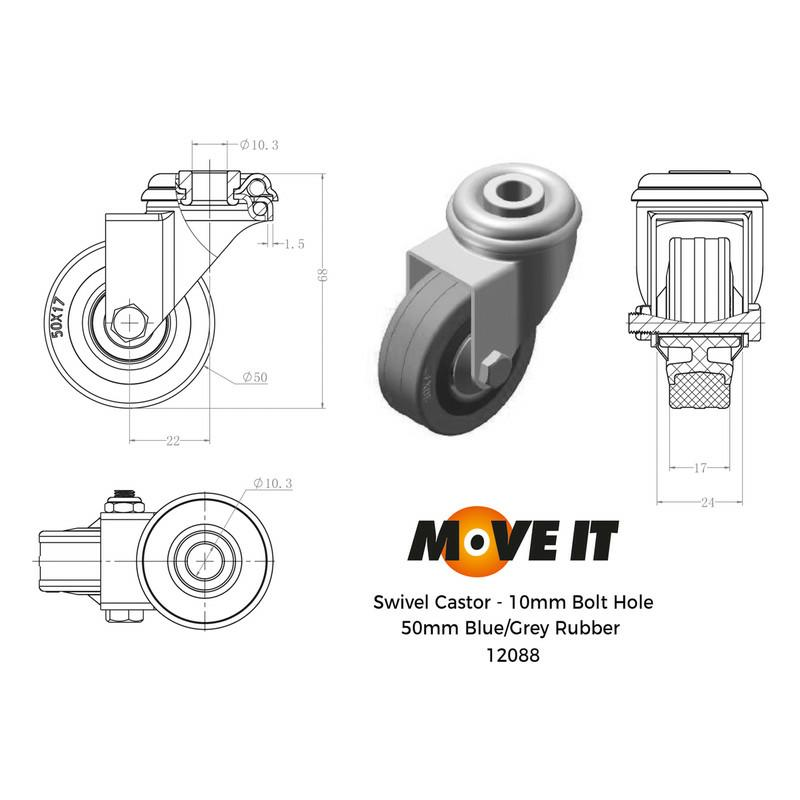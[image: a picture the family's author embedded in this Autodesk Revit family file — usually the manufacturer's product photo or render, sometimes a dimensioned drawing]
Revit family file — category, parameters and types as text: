
# Revit family: ThinkingWall Stor
name_source: partatom
category: Generic Models
units: mm (PartAtom-declared; Revit-internal decimal feet)

## family parameters
Always vertical = Yes
Can host rebar = No
Cut with Voids When Loaded = No
Maintain Annotation Orientation = No
Part Type = Normal
Room Calculation Point = No
Round Connector Dimension = Use Diameter
Shared = No
Work Plane-Based = No

## types (1)
- ThinkingWall® Stor
    Default Elevation = 0 mm  [stored 0 ft]
    Description = Double sided mobile whiteboard wall with open storage to optimise space. Part of the ThinkingWall® range for flexible breakout and meeting spaces.
    Length = 1200 mm
    Manufacturer = Logovisual LTD
    Model = ThinkingWall® Stor
    Stor = <By Category>
    URL = https://www.logovisual.com
    Width = 435 mm  [stored 1.42717 ft]

note: [stored X ft] marks values corroborated as IEEE doubles in the binary element streams (Revit-internal decimal feet)

## geometry (parser evidence)
native form markers: Sweep x10
no freeform markers — native parametric forms only
